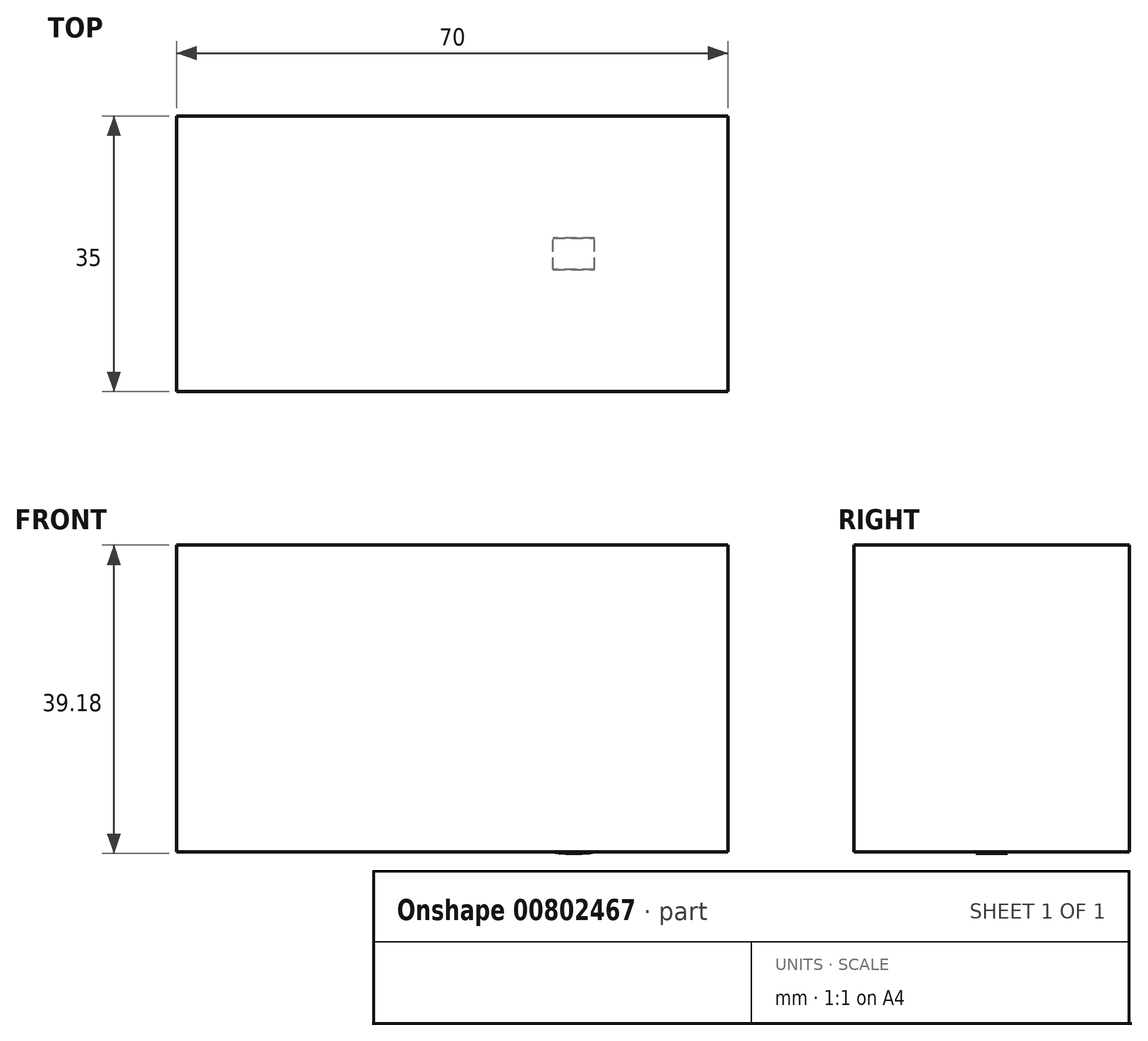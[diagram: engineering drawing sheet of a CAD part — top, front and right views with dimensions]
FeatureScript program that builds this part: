
annotation { "Feature Type Name" : "Feature", "Feature Type Description" : "" }
export const myFeature = defineFeature(function(context is Context, id is Id, definition is map)
    precondition{}
    {
        {
            var Q0;
            Q0=qCreatedBy(makeId("Front.planeOp"),FACE);
            var sketch = newSketch(context, id + "F0", { "sketchPlane" : qUnion([Q0])});
            skLineSegment(sketch, "E0.bottom", {"start": v(35, 19.5) * mm, "end": v(-35, 19.5) * mm});
            skLineSegment(sketch, "E0.top", {"start": v(35, -19.5) * mm, "end": v(-35, -19.5) * mm});
            skLineSegment(sketch, "E0.left", {"start": v(35, 19.5) * mm, "end": v(35, -19.5) * mm});
            skLineSegment(sketch, "E0.right", {"start": v(-35, 19.5) * mm, "end": v(-35, -19.5) * mm});
            skPoint(sketch, "E0.middle", {"position": v(0, 0) * mm});
            skSolve(sketch);
        }
        {
            var Q0;
            Q0=makeQuery(id+"F0.imprint","IMPRINT",FACE,{"disambiguationData":[TD([[makeQuery(id+"F0.imprint","IMPRINT",EDGE,{"derivedFrom":sQuery(id+"F0.wireOp",EDGE,"E0.bottom")}),1.0]])]});
            extrude(context, id + "F1", {"entities" : qUnion([Q0]), "endBound" : BoundingType.SYMMETRIC, "depth" : 35 * mm, "offsetDistance" : 25 * mm});
        }
        {
            var Q0;
            Q0=qCreatedBy(makeId("Front.planeOp"),FACE);
            var sketch = newSketch(context, id + "F2", { "sketchPlane" : qUnion([Q0])});
            skCircle(sketch, "E1", {"center": v(15.43, -0.18) * mm, "radius": 19.5 * mm});
            skPoint(sketch, "E1.first.point", {"position": v(17.33, 19.23) * mm});
            skPoint(sketch, "E1.second.point", {"position": v(34.92, 0) * mm});
            skPoint(sketch, "E1.third.point", {"position": v(19.57, -19.23) * mm});
            skSolve(sketch);
        }
        {
            var Q0;
            Q0 = qSketchRegion(id + "F2", true);
            extrude(context, id + "F3", {"entities" : qUnion([Q0]), "operationType" : NewBodyOperationType.ADD, "depth" : 2 * mm, "offsetDistance" : 25 * mm, "hasSecondDirection" : true, "secondDirectionOppositeDirection" : true, "secondDirectionDepth" : 2 * mm});
        }
    });
